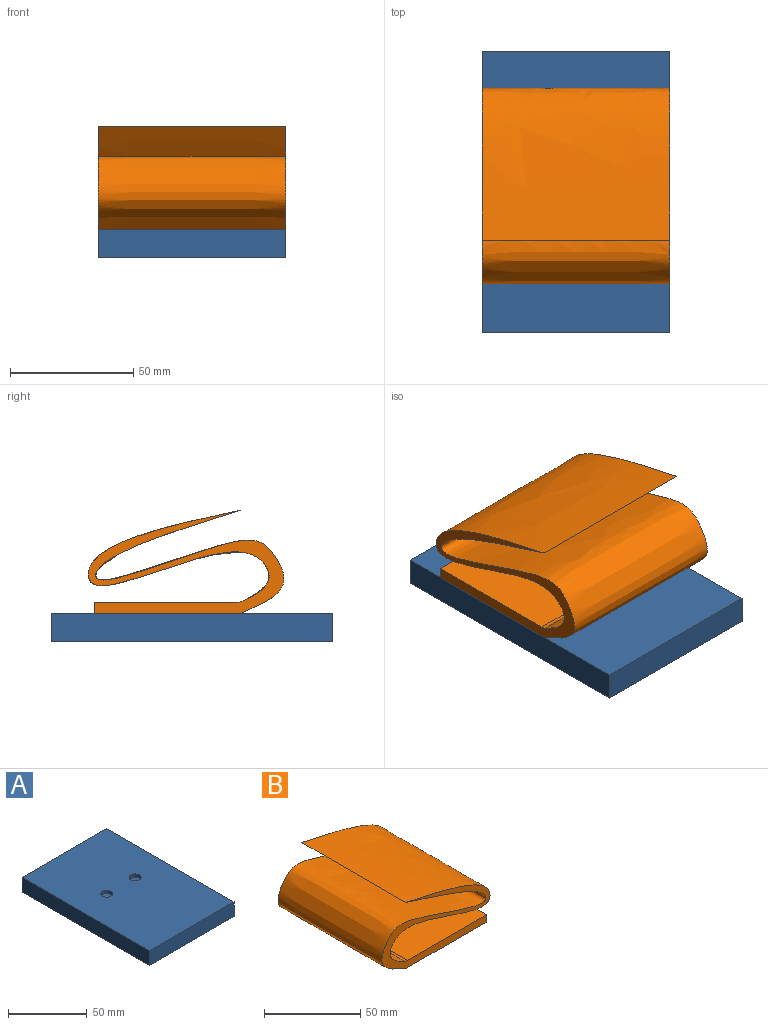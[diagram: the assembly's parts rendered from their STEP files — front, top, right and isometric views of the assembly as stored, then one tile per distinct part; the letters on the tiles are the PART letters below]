
ASSEMBLY  parts=2 mates=1
PART A: 18 faces, bbox 76.2x114.3x11.4 mm
  f0: plane 114.3x11.43mm, normal (-1,0,0), area 1306.4mm2, adj f1,f3,f4,f5
  f1: plane 114.3x76.2mm, normal (0,0,-1), area 8203mm2, adj f0,f2,f4,f5,f6,f8,f10,f12
  f2: plane 114.3x11.43mm, normal (1,0,0), area 1306.4mm2, adj f1,f3,f4,f5
  f3: plane 114.3x76.2mm, normal (0,0,1), area 8618.5mm2, adj f0,f2,f4,f5,f14,f16
  f4: plane 76.2x11.43mm, normal (0,-1,0), area 871mm2, adj f0,f1,f2,f3
  f5: plane 76.2x11.43mm, normal (0,1,0), area 871mm2, adj f0,f1,f2,f3
  f6: cylinder r=6.35mm len=12.7mm, axis (0,0,-1), area 253.4mm2, adj f1,f7
  f7: plane 12.7x12.7mm, normal (0,0,-1), area 126.7mm2, adj f6
  f8: cylinder r=6.35mm len=12.7mm, axis (0,0,-1), area 253.4mm2, adj f1,f9
  f9: plane 12.7x12.7mm, normal (0,0,-1), area 126.7mm2, adj f8
  f10: cylinder r=6.35mm len=12.7mm, axis (0,0,-1), area 253.4mm2, adj f1,f11
  f11: plane 12.7x12.7mm, normal (0,0,-1), area 126.7mm2, adj f10
  f12: cylinder r=6.35mm len=12.7mm, axis (0,0,-1), area 253.4mm2, adj f1,f13
  f13: plane 12.7x12.7mm, normal (0,0,-1), area 126.7mm2, adj f12
  f14: cylinder r=3.81mm len=7.62mm, axis (0,0,1), area 60.8mm2, adj f3,f15
  f15: plane 7.62x7.62mm, normal (0,0,1), area 45.6mm2, adj f14
  f16: cylinder r=3.81mm len=7.62mm, axis (0,0,1), area 60.8mm2, adj f3,f17
  f17: plane 7.62x7.62mm, normal (0,0,1), area 45.6mm2, adj f16
PART B: 16 faces, bbox 83.5x76.2x42 mm
  f0: extruded ~76.2x73.23mm, area 12591.9mm2, adj f1,f5,f6,f7,f10,f11,f12,f13
  f1: extruded ~76.2x76.09mm, area 13429.4mm2, adj f0,f2,f5,f6,f10,f12,f13,f14
  f2: plane 76.2x59.25mm, normal (0,0,-1), area 4423.5mm2, adj f1,f3,f5,f6,f8,f9
  f3: plane 76.2x4.61mm, normal (1,0,0), area 351.6mm2, adj f2,f4,f5,f6
  f4: plane 76.2x58.04mm, normal (0,0,1), area 4331.6mm2, adj f3,f5,f6,f7,f8,f9
  f5: plane 83.54x42.01mm, normal (0,-1,0), area 823.7mm2, adj f0,f1,f2,f3,f4,f7
  f6: plane 83.54x42.01mm, normal (0,1,0), area 823.7mm2, adj f0,f1,f2,f3,f4,f7
  f7: cylinder r=5.08mm len=76.2mm, axis (0,1,0), area 181.2mm2, adj f0,f4,f5,f6
  f8: cylinder r=3.81mm len=7.62mm, axis (0,0,-1), area 110.4mm2, adj f2,f4
  f9: cylinder r=3.81mm len=7.62mm, axis (0,0,-1), area 110.4mm2, adj f2,f4
  f10: plane 21.43x3.45mm, normal (0,1,0), area 38.8mm2, adj f0,f1,f11,f13,f14,f15
  f11: plane 14.09x7.69mm, normal (0,0,1), area 108.3mm2, adj f0,f10,f12
  f12: plane 21.43x3.45mm, normal (0,-1,0), area 38.8mm2, adj f0,f1,f11,f13,f14,f15
  f13: plane 14.09x7.63mm, normal (0,0,-1), area 107.4mm2, adj f0,f1,f10,f12
  f14: plane 14.09x2.9mm, normal (0,0,-1), area 40.9mm2, adj f1,f10,f12,f15
  f15: plane 14.09x0.7mm, normal (-1,0,0), area 9.9mm2, adj f0,f10,f12,f14
PLACE A t=(23.1,47.19,-24.64)mm
PLACE B rot(axis=(0,0,1),90deg) t=(-11.24,6.47,-39.17)mm
MATE fastened B.f9 <-> A.f14  axis (0,0,-1) through (14.16,-3.61,-32.49)mm
